# Revit family: wd-121_221bzmd5_50Hz
name_source: partatom
category: 機械設備
units: mm (PartAtom-declared; Revit-internal decimal feet)

## family parameters
OmniClass タイトル = Centrifugal Fans
OmniClass 番号 = 23.75.35.17.27
パーツ タイプ = 標準
ロード時にボイドで切り取り = いいえ
丸型コネクタ寸法 = 直径を使用
作業面ベース = いいえ
共有 = いいえ
常に垂直 = はい
部屋計算ポイント = はい

## types (2) — shared parameters
D1 = 472
D2 = 60  [stored 0.19685 ft]
Depth = 280  [stored 0.918635 ft]
Duct_D = 145  [stored 0.475722 ft]
Duct_Depth = 130  [stored 0.426509 ft]
Duct_H = 139
Duct_W = 120  [stored 0.393701 ft]
EAサイズ_D = 98  [stored 0.321522 ft]
H1 = 46  [stored 0.150919 ft]
Height = 194  [stored 0.636483 ft]
IfcExportAs = IfcFanType
IfcExportType = PROPELLORAXIAL
MAX静圧 = 0.0 Pa
MID静圧 = 0.0 Pa
MID風量 = 0.0 m³/h
MIN静圧 = 0.0 Pa
OmniClassCode = 23-33 31 19 11 15
URL = https://www.mitsubishielectric.co.jp
Uniclass2015Code = Pr_65_67_29_12
Uniclass2015Title = Centrifugal fans
Uniclass2015Version = Systems v1.9
W1 = 492  [stored 1.61417 ft]
Width = 400  [stored 1.31234 ft]
カバーマテリアル = 合成樹脂(白)
ダクト径 = 100 mm
マテリアル = 亜鉛メッキ鋼板
仕様書バージョン = Version1.0
企業コード = 108420
分類コード = 50052503100080
周波数 = 50 Hz
天吊金具_径 = 15  [stored 0.0492126 ft]
天吊金具_高さ = 97  [stored 0.318241 ft]
天吊金具ピッチ1 = 450  [stored 1.47638 ft]
天吊金具ピッチ2 = 450  [stored 1.47638 ft]
法定耐用年数 = 10
点検口 = はい
点検口_Depth = 450  [stored 1.47638 ft]
点検口離隔 = 150
相 = 1
積算_科目 = 2 換気設備
製品リリース年月 = 2022年6月1日
製品出荷対象 = 国内
製造元 = 三菱電機株式会社
設置方法 = カセット形
説明 = バス乾燥・暖房・換気システム 換気システム連動形
負荷分類 = 3_ファン類
運転質量 = 0.00 kg
電動機出力 = 0 W

## per-type parameters (varying)
| type | MAX風量 | MIN風量 | 価格 | 極数 | 消費電力 | 製品質量 | 質量 | 電圧 |
| WD-121BZMD5 | 170.0 m³/h | 120.0 m³/h | 111000 $ | 2 | 1330 W | 8.50 kg | 10.20 kg | 100 V |
| WD-221BZMD5 | 205.0 m³/h | 105.0 m³/h | 139400 $ | 3 | 2385 W | 9.00 kg | 10.80 kg | 200 V |

note: column(s) folded — value = type name in every type: モデル

note: [stored X ft] marks values corroborated as IEEE doubles in the binary element streams (Revit-internal decimal feet)
